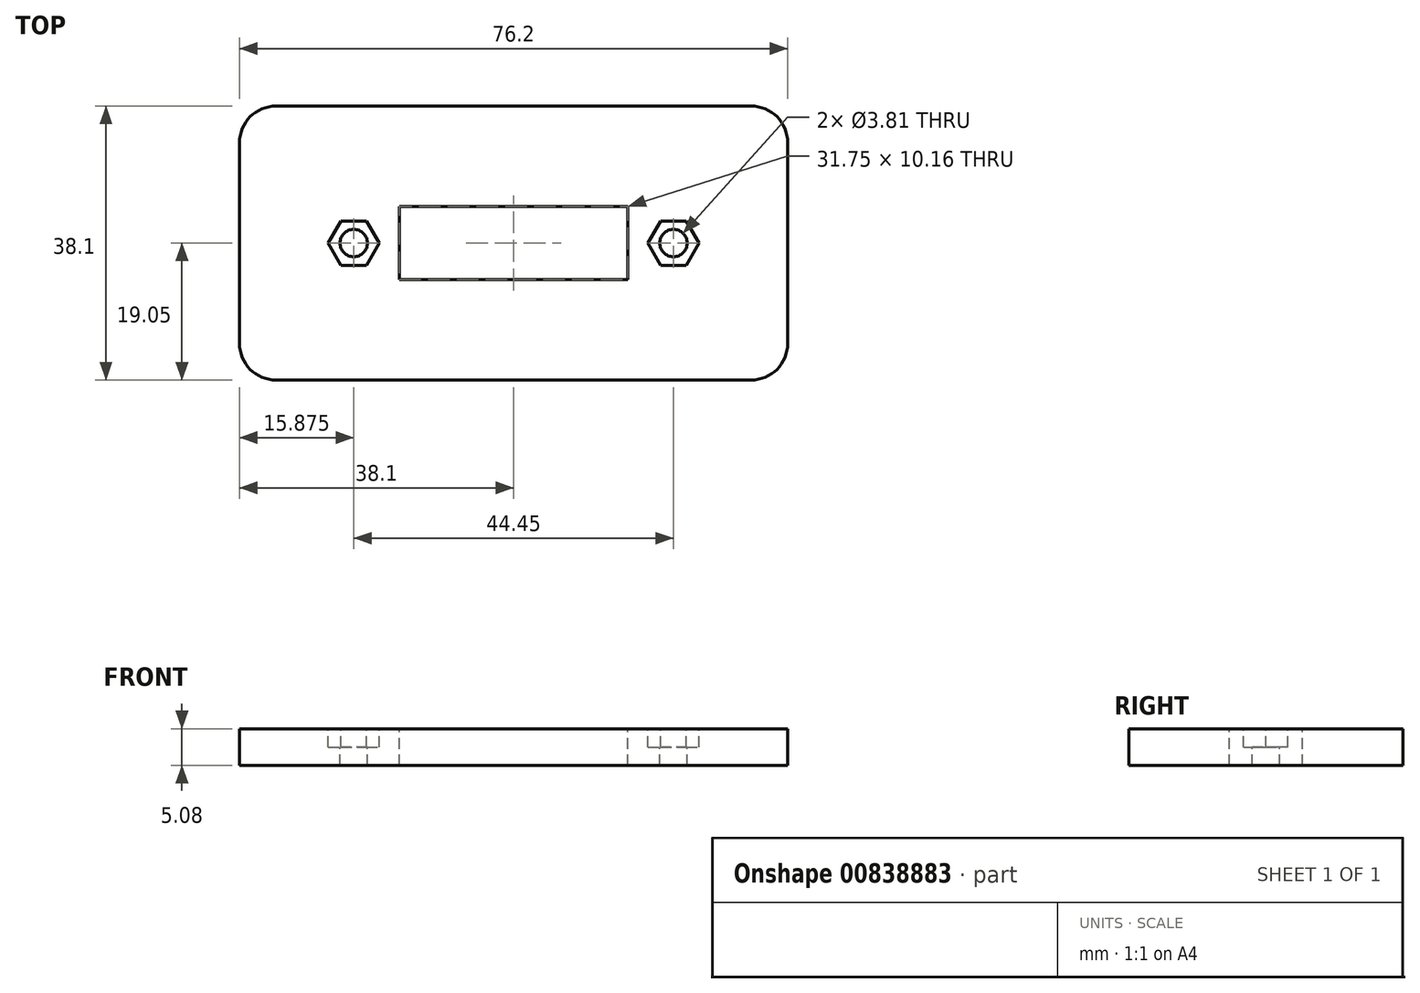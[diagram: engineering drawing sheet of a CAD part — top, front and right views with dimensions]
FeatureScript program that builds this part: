
annotation { "Feature Type Name" : "Feature", "Feature Type Description" : "" }
export const myFeature = defineFeature(function(context is Context, id is Id, definition is map)
    precondition{}
    {
        {
            var Q0;
            Q0=qCreatedBy(makeId("Top.planeOp"),FACE);
            var sketch = newSketch(context, id + "F0", { "sketchPlane" : qUnion([Q0])});
            skLineSegment(sketch, "E0.bottom", {"start": v(38.1, 19.05) * mm, "end": v(-38.1, 19.05) * mm});
            skLineSegment(sketch, "E0.top", {"start": v(38.1, -19.05) * mm, "end": v(-38.1, -19.05) * mm});
            skLineSegment(sketch, "E0.left", {"start": v(38.1, 19.05) * mm, "end": v(38.1, -19.05) * mm});
            skLineSegment(sketch, "E0.right", {"start": v(-38.1, 19.05) * mm, "end": v(-38.1, -19.05) * mm});
            skPoint(sketch, "E0.middle", {"position": v(0, 0) * mm});
            skSolve(sketch);
        }
        {
            var Q0;
            Q0=makeQuery(id+"F0.imprint","IMPRINT",FACE,{"disambiguationData":[TD([[makeQuery(id+"F0.imprint","IMPRINT",EDGE,{"derivedFrom":sQuery(id+"F0.wireOp",EDGE,"E0.bottom")}),1.0]])]});
            extrude(context, id + "F1", {"entities" : qUnion([Q0]), "depth" : 5.08 * mm, "offsetDistance" : 25.4 * mm});
        }
        {
            var Q0;
            Q0=makeQuery(id+"F1.opExtrude","CAP_FACE",FACE,{"disambiguationData":[OSD([sQuery(id+"F0.wireOp",EDGE,"E0.bottom"),sQuery(id+"F0.wireOp",EDGE,"E0.top"),sQuery(id+"F0.wireOp",EDGE,"E0.left"),sQuery(id+"F0.wireOp",EDGE,"E0.right")])],"isStart":false});
            var sketch = newSketch(context, id + "F2", { "sketchPlane" : qUnion([Q0])});
            skLineSegment(sketch, "E1.bottom", {"start": v(15.88, 5.08) * mm, "end": v(-15.88, 5.08) * mm});
            skLineSegment(sketch, "E1.top", {"start": v(15.88, -5.08) * mm, "end": v(-15.88, -5.08) * mm});
            skLineSegment(sketch, "E1.left", {"start": v(15.88, 5.08) * mm, "end": v(15.88, -5.08) * mm});
            skLineSegment(sketch, "E1.right", {"start": v(-15.88, 5.08) * mm, "end": v(-15.88, -5.08) * mm});
            skPoint(sketch, "E1.middle", {"position": v(0, 0) * mm});
            skSolve(sketch);
        }
        {
            var Q0;
            Q0=makeQuery(id+"F2.imprint","IMPRINT",FACE,{"disambiguationData":[TD([[makeQuery(id+"F2.imprint","IMPRINT",EDGE,{"derivedFrom":sQuery(id+"F2.wireOp",EDGE,"E1.bottom")}),1.0]])]});
            var Q1;
            Q1=makeQuery(id+"F1.opExtrude","CAP_FACE",FACE,{"disambiguationData":[OSD([sQuery(id+"F0.wireOp",EDGE,"E0.bottom"),sQuery(id+"F0.wireOp",EDGE,"E0.top"),sQuery(id+"F0.wireOp",EDGE,"E0.left"),sQuery(id+"F0.wireOp",EDGE,"E0.right")])],"isStart":true});
            extrude(context, id + "F3", {"entities" : qUnion([Q0]), "operationType" : NewBodyOperationType.REMOVE, "endBound" : BoundingType.UP_TO_SURFACE, "oppositeDirection" : true, "depth" : 25.4 * mm, "endBoundEntityFace" : qUnion([Q1]), "offsetDistance" : 25.4 * mm});
        }
        {
            var Q0;
            Q0=makeQuery(id+"F1.opExtrude","CAP_FACE",FACE,{"disambiguationData":[OSD([sQuery(id+"F0.wireOp",EDGE,"E0.bottom"),sQuery(id+"F0.wireOp",EDGE,"E0.top"),sQuery(id+"F0.wireOp",EDGE,"E0.left"),sQuery(id+"F0.wireOp",EDGE,"E0.right")])],"isStart":false});
            var sketch = newSketch(context, id + "F4", { "sketchPlane" : qUnion([Q0])});
            skCircle(sketch, "E2", {"center": v(-22.23, 0) * mm, "radius": 1.9 * mm});
            skCircle(sketch, "E3", {"center": v(22.23, 0) * mm, "radius": 1.9 * mm});
            skLineSegment(sketch, "E4", {"start": v(-22.23, 0) * mm, "end": v(22.23, 0) * mm});
            skPoint(sketch, "E5", {"position": v(0, 0) * mm});
            skSolve(sketch);
        }
        {
            var Q0;
            Q0=makeQuery(id+"F4.imprint","IMPRINT",FACE,{"disambiguationData":[TD([[makeQuery(id+"F4.imprint","IMPRINT",EDGE,{"derivedFrom":sQuery(id+"F4.wireOp",EDGE,"E2")}),1.0]])]});
            var Q1;
            Q1=makeQuery(id+"F4.imprint","IMPRINT",FACE,{"disambiguationData":[TD([[makeQuery(id+"F4.imprint","IMPRINT",EDGE,{"derivedFrom":sQuery(id+"F4.wireOp",EDGE,"E3")}),1.0]])]});
            var Q2;
            Q2=makeQuery(id+"F1.opExtrude","CAP_FACE",FACE,{"disambiguationData":[OSD([sQuery(id+"F0.wireOp",EDGE,"E0.bottom"),sQuery(id+"F0.wireOp",EDGE,"E0.top"),sQuery(id+"F0.wireOp",EDGE,"E0.left"),sQuery(id+"F0.wireOp",EDGE,"E0.right")])],"isStart":true});
            extrude(context, id + "F5", {"entities" : qUnion([Q0, Q1]), "operationType" : NewBodyOperationType.REMOVE, "endBound" : BoundingType.UP_TO_SURFACE, "oppositeDirection" : true, "depth" : 25.4 * mm, "endBoundEntityFace" : qUnion([Q2]), "offsetDistance" : 25.4 * mm});
        }
        {
            var Q0;
            Q0=makeQuery(id+"F1.opExtrude","CAP_FACE",FACE,{"disambiguationData":[OSD([sQuery(id+"F0.wireOp",EDGE,"E0.bottom"),sQuery(id+"F0.wireOp",EDGE,"E0.top"),sQuery(id+"F0.wireOp",EDGE,"E0.left"),sQuery(id+"F0.wireOp",EDGE,"E0.right")])],"isStart":false});
            var sketch = newSketch(context, id + "F6", { "sketchPlane" : qUnion([Q0])});
            skCircle(sketch, "E6.cCircle", {"center": v(-22.23, 0) * mm, "radius": 3.08 * mm, "construction": true});
            skLineSegment(sketch, "E6.0", {"start": v(-20.45, 3.08) * mm, "end": v(-18.67, 0) * mm});
            skLineSegment(sketch, "E6.1", {"start": v(-18.67, 0) * mm, "end": v(-20.45, -3.08) * mm});
            skLineSegment(sketch, "E6.2", {"start": v(-20.45, -3.08) * mm, "end": v(-24, -3.08) * mm});
            skLineSegment(sketch, "E6.3", {"start": v(-24, -3.08) * mm, "end": v(-25.78, 0) * mm});
            skLineSegment(sketch, "E6.4", {"start": v(-25.78, 0) * mm, "end": v(-24, 3.08) * mm});
            skLineSegment(sketch, "E6.5", {"start": v(-24, 3.08) * mm, "end": v(-20.45, 3.08) * mm});
            skPoint(sketch, "E6.0.midPoint", {"position": v(-19.56, 1.54) * mm});
            skCircle(sketch, "E7.cCircle", {"center": v(22.23, 0) * mm, "radius": 3.08 * mm, "construction": true});
            skLineSegment(sketch, "E7.0", {"start": v(24, 3.08) * mm, "end": v(25.78, 0) * mm});
            skLineSegment(sketch, "E7.1", {"start": v(25.78, 0) * mm, "end": v(24, -3.08) * mm});
            skLineSegment(sketch, "E7.2", {"start": v(24, -3.08) * mm, "end": v(20.45, -3.08) * mm});
            skLineSegment(sketch, "E7.3", {"start": v(20.45, -3.08) * mm, "end": v(18.67, 0) * mm});
            skLineSegment(sketch, "E7.4", {"start": v(18.67, 0) * mm, "end": v(20.45, 3.08) * mm});
            skLineSegment(sketch, "E7.5", {"start": v(20.45, 3.08) * mm, "end": v(24, 3.08) * mm});
            skPoint(sketch, "E7.0.midPoint", {"position": v(24.9, 1.54) * mm});
            skSolve(sketch);
        }
        {
            var Q0;
            Q0=makeQuery(id+"F6.imprint","IMPRINT",FACE,{"disambiguationData":[TD([[makeQuery(id+"F6.imprint","IMPRINT",EDGE,{"derivedFrom":sQuery(id+"F6.wireOp",EDGE,"E6.0")}),-1.0]])]});
            var Q1;
            Q1=makeQuery(id+"F6.imprint","IMPRINT",FACE,{"disambiguationData":[TD([[makeQuery(id+"F6.imprint","IMPRINT",EDGE,{"derivedFrom":sQuery(id+"F6.wireOp",EDGE,"E7.0")}),-1.0]])]});
            extrude(context, id + "F7", {"entities" : qUnion([Q0, Q1]), "operationType" : NewBodyOperationType.REMOVE, "oppositeDirection" : true, "depth" : 2.54 * mm, "offsetDistance" : 25.4 * mm});
        }
        {
            var Q0;
            Q0=makeQuery(id+"F1.opExtrude","SWEPT_EDGE",EDGE,{"disambiguationData":[OSD([sQuery(id+"F0.wireOp",EDGE,"E0.top"),sQuery(id+"F0.wireOp",EDGE,"E0.left")])]});
            var Q1;
            Q1=makeQuery(id+"F1.opExtrude","SWEPT_EDGE",EDGE,{"disambiguationData":[OSD([sQuery(id+"F0.wireOp",EDGE,"E0.bottom"),sQuery(id+"F0.wireOp",EDGE,"E0.left")])]});
            var Q2;
            Q2=makeQuery(id+"F1.opExtrude","SWEPT_EDGE",EDGE,{"disambiguationData":[OSD([sQuery(id+"F0.wireOp",EDGE,"E0.bottom"),sQuery(id+"F0.wireOp",EDGE,"E0.right")])]});
            var Q3;
            Q3=makeQuery(id+"F1.opExtrude","SWEPT_EDGE",EDGE,{"disambiguationData":[OSD([sQuery(id+"F0.wireOp",EDGE,"E0.top"),sQuery(id+"F0.wireOp",EDGE,"E0.right")])]});
            fillet(context, id + "F8", {"entities" : qUnion([Q0, Q1, Q2, Q3]), "radius" : 5.08 * mm, "tangentPropagation" : true, "allowEdgeOverflow" : false});
        }
    });
